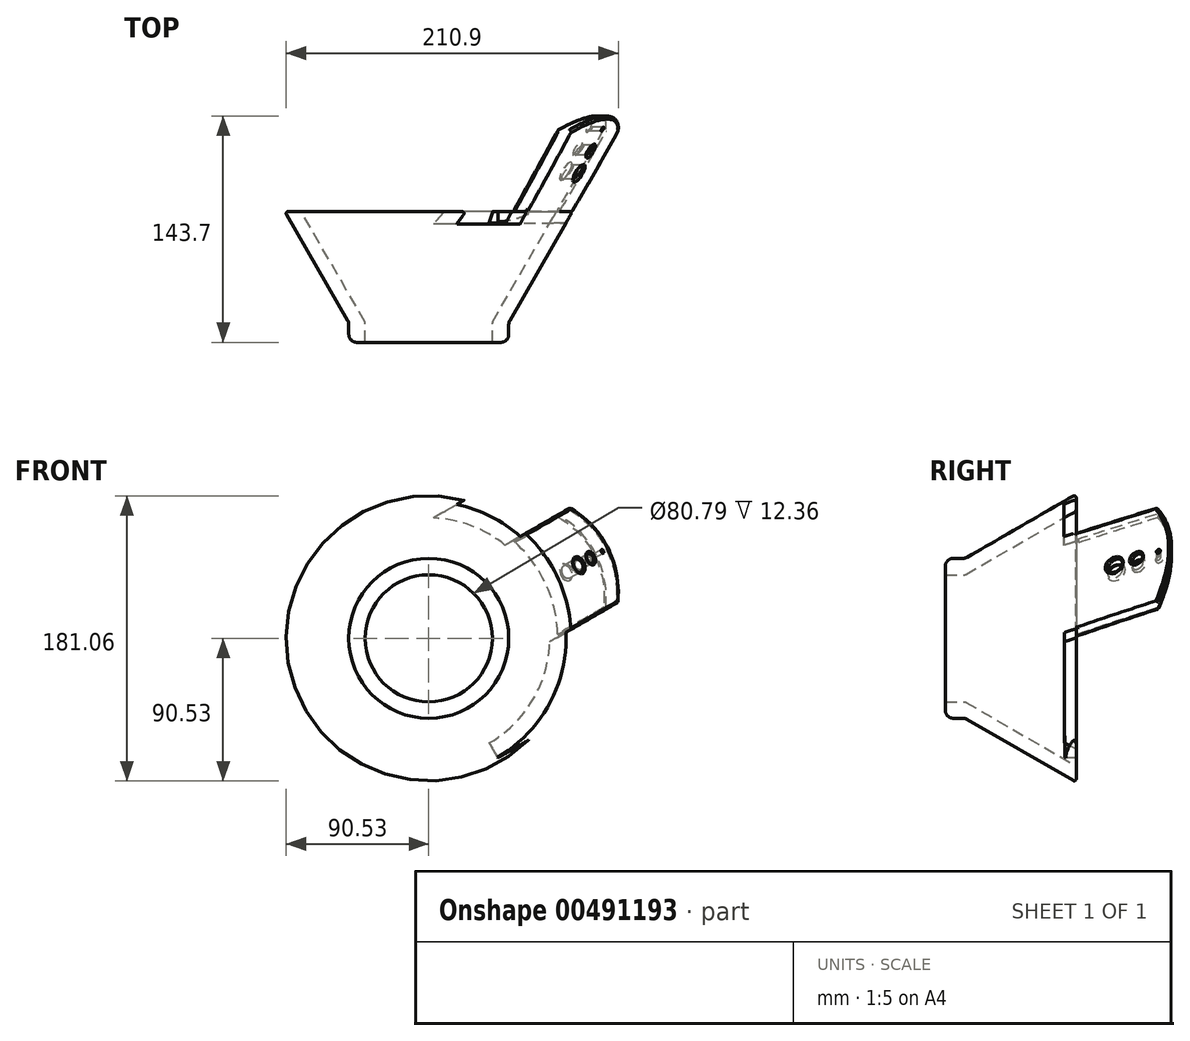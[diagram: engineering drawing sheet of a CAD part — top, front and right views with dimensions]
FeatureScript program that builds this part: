
annotation { "Feature Type Name" : "Feature", "Feature Type Description" : "" }
export const myFeature = defineFeature(function(context is Context, id is Id, definition is map)
    precondition{}
    {
        {
            var Q0;
            Q0=qCreatedBy(makeId("Top.planeOp"),FACE);
            var sketch = newSketch(context, id + "F0", { "sketchPlane" : qUnion([Q0])});
            skLineSegment(sketch, "E0", {"start": v(50.8, -12.7) * mm, "end": v(50.8, 0) * mm});
            skLineSegment(sketch, "E1", {"start": v(50.8, 0) * mm, "end": v(91.46, 70.42) * mm});
            skLineSegment(sketch, "E2", {"start": v(81.05, 70.42) * mm, "end": v(40.4, 0) * mm});
            skLineSegment(sketch, "E3", {"start": v(81.05, 70.42) * mm, "end": v(91.46, 70.42) * mm});
            skLineSegment(sketch, "E4", {"start": v(0, 0) * mm, "end": v(0, -12.7) * mm});
            skLineSegment(sketch, "E5", {"start": v(40.4, 0) * mm, "end": v(40.4, -12.7) * mm});
            skLineSegment(sketch, "E6", {"start": v(40.4, -12.7) * mm, "end": v(50.8, -12.7) * mm});
            skLineSegment(sketch, "E7", {"start": v(32.23, 0) * mm, "end": v(60.67, 0) * mm, "construction": true});
            skSolve(sketch);
        }
        {
            var Q0;
            Q0=makeQuery(id+"F0.imprint","IMPRINT",FACE,{"disambiguationData":[TD([[makeQuery(id+"F0.imprint","IMPRINT",EDGE,{"derivedFrom":sQuery(id+"F0.wireOp",EDGE,"cES71L1K-G2Gt-OJuJ-8Dwa-AGLuiCApIHVb")}),1.0]])]});
            var Q1;
            Q1=makeQuery(id+"F0.imprint","IMPRINT",FACE,{"disambiguationData":[TD([[makeQuery(id+"F0.imprint","IMPRINT",EDGE,{"derivedFrom":sQuery(id+"F0.wireOp",EDGE,"E0")}),1.0]])]});
            var Q2;
            {var subQ0=sQuery(id+"F0.wireOp",EDGE,"E1");Q2=makeQuery(id+"F0.imprint","IMPRINT",FACE,{"disambiguationData":[TD([[makeQuery(id+"F0.imprint","IMPRINT",EDGE,{"derivedFrom":subQ0}),1.0]])]});}
            var Q3;
            Q3=sQuery(id+"F0.wireOp",EDGE,"E4");
            revolve(context, id + "F1", {"entities" : qUnion([Q0, Q1, Q2]), "axis" : qUnion([Q3]), "revolveType" : RevolveType.FULL});
        }
        {
            var Q0;
            Q0=qCreatedBy(makeId("Top.planeOp"),FACE);
            var sketch = newSketch(context, id + "F2", { "sketchPlane" : qUnion([Q0])});
            skLineSegment(sketch, "E8", {"start": v(91.31, 70.36) * mm, "end": v(128.65, 131.35) * mm});
            skLineSegment(sketch, "E9", {"start": v(80.94, 70.29) * mm, "end": v(118.28, 131.27) * mm});
            skLineSegment(sketch, "E10", {"start": v(118.28, 131.27) * mm, "end": v(128.65, 131.35) * mm});
            skLineSegment(sketch, "E11", {"start": v(80.94, 70.29) * mm, "end": v(91.31, 70.36) * mm});
            skSolve(sketch);
        }
        {
            var Q0;
            Q0=makeQuery(id+"F2.imprint","IMPRINT",FACE,{"disambiguationData":[TD([[makeQuery(id+"F2.imprint","IMPRINT",EDGE,{"derivedFrom":sQuery(id+"F2.wireOp",EDGE,"E8")}),1.0]])]});
            var Q1;
            Q1=sQuery(id+"F0.wireOp",EDGE,"E4");
            revolve(context, id + "F3", {"entities" : qUnion([Q0]), "axis" : qUnion([Q1]), "revolveType" : RevolveType.ONE_DIRECTION, "angle" : 50 * degree});
        }
        {
            var Q0;
            Q0=makeQuery(id+"F3.opRevolve","SWEPT_FACE",FACE,{"disambiguationData":[OSD([sQuery(id+"F2.wireOp",EDGE,"E8")])]});
            cPlane(context, id + "F4", {"entities" : qUnion([Q0]), "cplaneType" : CPlaneType.LINE_ANGLE, "offset" : 25.4 * mm, "angle" : 60 * degree, "width" : 152.4 * mm, "height" : 152.4 * mm});
        }
        {
            var Q0;
            Q0=qCreatedBy(id+"F4.planeOp",FACE);
            var sketch = newSketch(context, id + "F5", { "sketchPlane" : qUnion([Q0])});
            skLineSegment(sketch, "E12", {"start": v(63.06, -40.28) * mm, "end": v(151.31, -40.28) * mm});
            skLineSegment(sketch, "E13", {"start": v(151.31, -40.28) * mm, "end": v(151.31, -87.68) * mm});
            skLineSegment(sketch, "E14", {"start": v(151.31, -87.68) * mm, "end": v(63.1, -87.68) * mm});
            skLineSegment(sketch, "E15", {"start": v(63.1, -87.68) * mm, "end": v(63.06, -40.28) * mm});
            skLineSegment(sketch, "E16.bottom", {"start": v(62.53, 26.93) * mm, "end": v(158.16, 26.93) * mm});
            skLineSegment(sketch, "E16.top", {"start": v(62.53, 64.74) * mm, "end": v(158.16, 64.74) * mm});
            skLineSegment(sketch, "E16.left", {"start": v(62.53, 26.93) * mm, "end": v(62.53, 64.74) * mm});
            skLineSegment(sketch, "E16.right", {"start": v(158.16, 26.93) * mm, "end": v(158.16, 64.74) * mm});
            skArc(sketch, "E17", {"start": v(122.36, -40.28) * mm, "mid": v(131, -6.64) * mm, "end": v(122.02, 26.93) * mm});
            skLineSegment(sketch, "E18", {"start": v(63.06, -40.28) * mm, "end": v(62.53, 26.93) * mm});
            skLineSegment(sketch, "E19", {"start": v(131, -7.32) * mm, "end": v(62.8, -7.32) * mm, "construction": true});
            skPoint(sketch, "E19.startSnap0", {"position": v(131, -6.64) * mm});
            skCircle(sketch, "E20", {"center": v(122.67, -7.32) * mm, "radius": 1.27 * mm});
            skCircle(sketch, "E21", {"center": v(109.47, -7.32) * mm, "radius": 3.18 * mm});
            skCircle(sketch, "E22", {"center": v(95.29, -7.32) * mm, "radius": 4.45 * mm});
            skLineSegment(sketch, "E23", {"start": v(139.78, -40.28) * mm, "end": v(139.78, 26.93) * mm});
            skSolve(sketch);
        }
        {
            var Q0;
            {var subQ0=sQuery(id+"F5.wireOp",EDGE,"E13");Q0=makeQuery(id+"F5.imprint","IMPRINT",FACE,{"disambiguationData":[TD([[makeQuery(id+"F5.imprint","IMPRINT",EDGE,{"derivedFrom":subQ0}),-1.0]])]});}
            var Q1;
            {var subQ0=sQuery(id+"F5.wireOp",EDGE,"E17");Q1=makeQuery(id+"F5.imprint","IMPRINT",FACE,{"disambiguationData":[TD([[makeQuery(id+"F5.imprint","IMPRINT",EDGE,{"derivedFrom":subQ0}),-1.0]])]});}
            var Q2;
            Q2=makeQuery(id+"F5.imprint","IMPRINT",FACE,{"disambiguationData":[TD([[makeQuery(id+"F5.imprint","IMPRINT",EDGE,{"derivedFrom":sQuery(id+"F5.wireOp",EDGE,"E20")}),1.0]])]});
            var Q3;
            Q3=makeQuery(id+"F5.imprint","IMPRINT",FACE,{"disambiguationData":[TD([[makeQuery(id+"F5.imprint","IMPRINT",EDGE,{"derivedFrom":sQuery(id+"F5.wireOp",EDGE,"E21")}),1.0]])]});
            var Q4;
            Q4=makeQuery(id+"F5.imprint","IMPRINT",FACE,{"disambiguationData":[TD([[makeQuery(id+"F5.imprint","IMPRINT",EDGE,{"derivedFrom":sQuery(id+"F5.wireOp",EDGE,"E22")}),1.0]])]});
            var Q5;
            Q5=makeQuery(id+"F5.imprint","IMPRINT",FACE,{"disambiguationData":[TD([[makeQuery(id+"F5.imprint","IMPRINT",EDGE,{"derivedFrom":sQuery(id+"F5.wireOp",EDGE,"E16.top")}),-1.0]])]});
            extrude(context, id + "F6", {"entities" : qUnion([Q0, Q1, Q2, Q3, Q4, Q5]), "operationType" : NewBodyOperationType.REMOVE, "depth" : 508 * mm});
        }
        {
            var Q0;
            Q0=makeQuery(id+"F1.opRevolve","SWEPT_EDGE",EDGE,{"disambiguationData":[OSD([sQuery(id+"F0.wireOp",EDGE,"cES71L1K-G2Gt-OJuJ-8Dwa-AGLuiCApIHVb"),sQuery(id+"F0.wireOp",EDGE,"E0")])]});
            fillet(context, id + "F7", {"entities" : qUnion([Q0]), "radius" : 5.08 * mm, "tangentPropagation" : true, "allowEdgeOverflow" : false});
        }
        {
            var Q0;
            Q0=makeQuery(id+"F6.boolean.opBoolean","INTERSECT",EDGE,{"derivedFrom":[makeQuery(id+"F3.opRevolve","SWEPT_FACE",FACE,{"disambiguationData":[OSD([sQuery(id+"F2.wireOp",EDGE,"E9")])]}),makeQuery(id+"F6.opExtrude","SWEPT_FACE",FACE,{"disambiguationData":[OSD([sQuery(id+"F5.wireOp",EDGE,"E22")])]})]});
            var Q1;
            Q1=makeQuery(id+"F6.boolean.opBoolean","INTERSECT",EDGE,{"derivedFrom":[makeQuery(id+"F3.opRevolve","SWEPT_FACE",FACE,{"disambiguationData":[OSD([sQuery(id+"F2.wireOp",EDGE,"E9")])]}),makeQuery(id+"F6.opExtrude","SWEPT_FACE",FACE,{"disambiguationData":[OSD([sQuery(id+"F5.wireOp",EDGE,"E21")])]})]});
            var Q2;
            Q2=makeQuery(id+"F6.boolean.opBoolean","INTERSECT",EDGE,{"derivedFrom":[makeQuery(id+"F3.opRevolve","SWEPT_FACE",FACE,{"disambiguationData":[OSD([sQuery(id+"F2.wireOp",EDGE,"E9")])]}),makeQuery(id+"F6.opExtrude","SWEPT_FACE",FACE,{"disambiguationData":[OSD([sQuery(id+"F5.wireOp",EDGE,"E20")])]})]});
            fillet(context, id + "F8", {"entities" : qUnion([Q0, Q1, Q2]), "radius" : 1.27 * mm, "tangentPropagation" : true, "allowEdgeOverflow" : false});
        }
        {
            var Q0;
            Q0=makeQuery(id+"F6.boolean.opBoolean","INTERSECT",EDGE,{"derivedFrom":[makeQuery(id+"F3.opRevolve","SWEPT_FACE",FACE,{"disambiguationData":[OSD([sQuery(id+"F2.wireOp",EDGE,"E8")])]}),makeQuery(id+"F6.opExtrude","SWEPT_FACE",FACE,{"disambiguationData":[OSD([sQuery(id+"F5.wireOp",EDGE,"E21")])]})]});
            var Q1;
            Q1=makeQuery(id+"F6.boolean.opBoolean","INTERSECT",EDGE,{"derivedFrom":[makeQuery(id+"F3.opRevolve","SWEPT_FACE",FACE,{"disambiguationData":[OSD([sQuery(id+"F2.wireOp",EDGE,"E8")])]}),makeQuery(id+"F6.opExtrude","SWEPT_FACE",FACE,{"disambiguationData":[OSD([sQuery(id+"F5.wireOp",EDGE,"E22")])]})]});
            fillet(context, id + "F9", {"entities" : qUnion([Q0, Q1]), "radius" : 1.27 * mm, "tangentPropagation" : true, "allowEdgeOverflow" : false});
        }
        {
            var Q0;
            Q0=makeQuery(id+"F6.boolean.opBoolean","INTERSECT",EDGE,{"derivedFrom":[makeQuery(id+"F3.opRevolve","SWEPT_FACE",FACE,{"disambiguationData":[OSD([sQuery(id+"F2.wireOp",EDGE,"E9")])]}),makeQuery(id+"F6.opExtrude","SWEPT_FACE",FACE,{"disambiguationData":[OSD([sQuery(id+"F5.wireOp",EDGE,"E17")])]})]});
            var Q1;
            Q1=makeQuery(id+"F6.boolean.opBoolean","INTERSECT",EDGE,{"derivedFrom":[makeQuery(id+"F3.opRevolve","SWEPT_FACE",FACE,{"disambiguationData":[OSD([sQuery(id+"F2.wireOp",EDGE,"E8")])]}),makeQuery(id+"F6.opExtrude","SWEPT_FACE",FACE,{"disambiguationData":[OSD([sQuery(id+"F5.wireOp",EDGE,"E17")])]})]});
            fillet(context, id + "F10", {"entities" : qUnion([Q0, Q1]), "radius" : 1.27 * mm, "tangentPropagation" : true, "allowEdgeOverflow" : false});
        }
        {
            var Q0;
            Q0=makeQuery(id+"F1.opRevolve","SWEPT_EDGE",EDGE,{"disambiguationData":[OSD([sQuery(id+"F0.wireOp",EDGE,"E2"),sQuery(id+"F0.wireOp",EDGE,"mVb7F2rA-TQsv-eaZc-jl8x-4uv2z7IkLspJ")])]});
            var Q1;
            Q1=makeQuery(id+"F1.opRevolve","SWEPT_EDGE",EDGE,{"disambiguationData":[OSD([sQuery(id+"F0.wireOp",EDGE,"E2"),sQuery(id+"F0.wireOp",EDGE,"E3")])]});
            var Q2;
            Q2=makeQuery(id+"F1.opRevolve","SWEPT_EDGE",EDGE,{"disambiguationData":[OSD([sQuery(id+"F0.wireOp",EDGE,"E1"),sQuery(id+"F0.wireOp",EDGE,"E3")])]});
            fillet(context, id + "F11", {"entities" : qUnion([Q0, Q1, Q2]), "radius" : 1.27 * mm, "tangentPropagation" : true, "allowEdgeOverflow" : false});
        }
        {
            var Q0;
            {var subQ0=sQuery(id+"F5.wireOp",EDGE,"E16.bottom");Q0=makeQuery(id+"F6.boolean.opBoolean","INTERSECT",EDGE,{"derivedFrom":[makeQuery(id+"F3.opRevolve","SWEPT_FACE",FACE,{"disambiguationData":[OSD([sQuery(id+"F2.wireOp",EDGE,"E8")])]}),makeQuery(id+"F6.opExtrude","SWEPT_FACE",FACE,{"disambiguationData":[OSD([subQ0]),TDD([makeQuery(id+"F5.imprint","IMPRINT",EDGE,{"disambiguationData":[TD([[makeQuery(id+"F5.imprint","INTERSECT",VERTEX,{"derivedFrom":[subQ0,sQuery(id+"F5.wireOp",EDGE,"E17")]}),1.0]])],"derivedFrom":subQ0})])]})]});}
            var Q1;
            {var subQ0=sQuery(id+"F5.wireOp",EDGE,"E16.bottom");Q1=makeQuery(id+"F6.boolean.opBoolean","INTERSECT",EDGE,{"derivedFrom":[makeQuery(id+"F3.opRevolve","SWEPT_FACE",FACE,{"disambiguationData":[OSD([sQuery(id+"F2.wireOp",EDGE,"E9")])]}),makeQuery(id+"F6.opExtrude","SWEPT_FACE",FACE,{"disambiguationData":[OSD([subQ0]),TDD([makeQuery(id+"F5.imprint","IMPRINT",EDGE,{"disambiguationData":[TD([[makeQuery(id+"F5.imprint","INTERSECT",VERTEX,{"derivedFrom":[subQ0,sQuery(id+"F5.wireOp",EDGE,"E17")]}),1.0]])],"derivedFrom":subQ0})])]})]});}
            var Q2;
            {var subQ0=sQuery(id+"F5.wireOp",EDGE,"E12");Q2=makeQuery(id+"F6.boolean.opBoolean","INTERSECT",EDGE,{"derivedFrom":[makeQuery(id+"F3.opRevolve","SWEPT_FACE",FACE,{"disambiguationData":[OSD([sQuery(id+"F2.wireOp",EDGE,"E9")])]}),makeQuery(id+"F6.opExtrude","SWEPT_FACE",FACE,{"disambiguationData":[OSD([subQ0]),TDD([makeQuery(id+"F5.imprint","IMPRINT",EDGE,{"disambiguationData":[TD([[makeQuery(id+"F5.imprint","INTERSECT",VERTEX,{"derivedFrom":[subQ0,sQuery(id+"F5.wireOp",EDGE,"E17")]}),1.0]])],"derivedFrom":subQ0})])]})]});}
            var Q3;
            {var subQ0=sQuery(id+"F5.wireOp",EDGE,"E12");Q3=makeQuery(id+"F6.boolean.opBoolean","INTERSECT",EDGE,{"derivedFrom":[makeQuery(id+"F3.opRevolve","SWEPT_FACE",FACE,{"disambiguationData":[OSD([sQuery(id+"F2.wireOp",EDGE,"E8")])]}),makeQuery(id+"F6.opExtrude","SWEPT_FACE",FACE,{"disambiguationData":[OSD([subQ0]),TDD([makeQuery(id+"F5.imprint","IMPRINT",EDGE,{"disambiguationData":[TD([[makeQuery(id+"F5.imprint","INTERSECT",VERTEX,{"derivedFrom":[subQ0,sQuery(id+"F5.wireOp",EDGE,"E17")]}),1.0]])],"derivedFrom":subQ0})])]})]});}
            fillet(context, id + "F12", {"entities" : qUnion([Q0, Q1, Q2, Q3]), "radius" : 1.27 * mm, "tangentPropagation" : true, "allowEdgeOverflow" : false});
        }
        {
            var Q0;
            Q0=makeQuery(id+"F3.opRevolve","SWEPT_EDGE",EDGE,{"disambiguationData":[OSD([sQuery(id+"F2.wireOp",EDGE,"E8"),sQuery(id+"F2.wireOp",EDGE,"E11")])]});
            fillet(context, id + "F13", {"entities" : qUnion([Q0]), "radius" : 1.27 * mm, "tangentPropagation" : true, "allowEdgeOverflow" : false});
        }
    });
